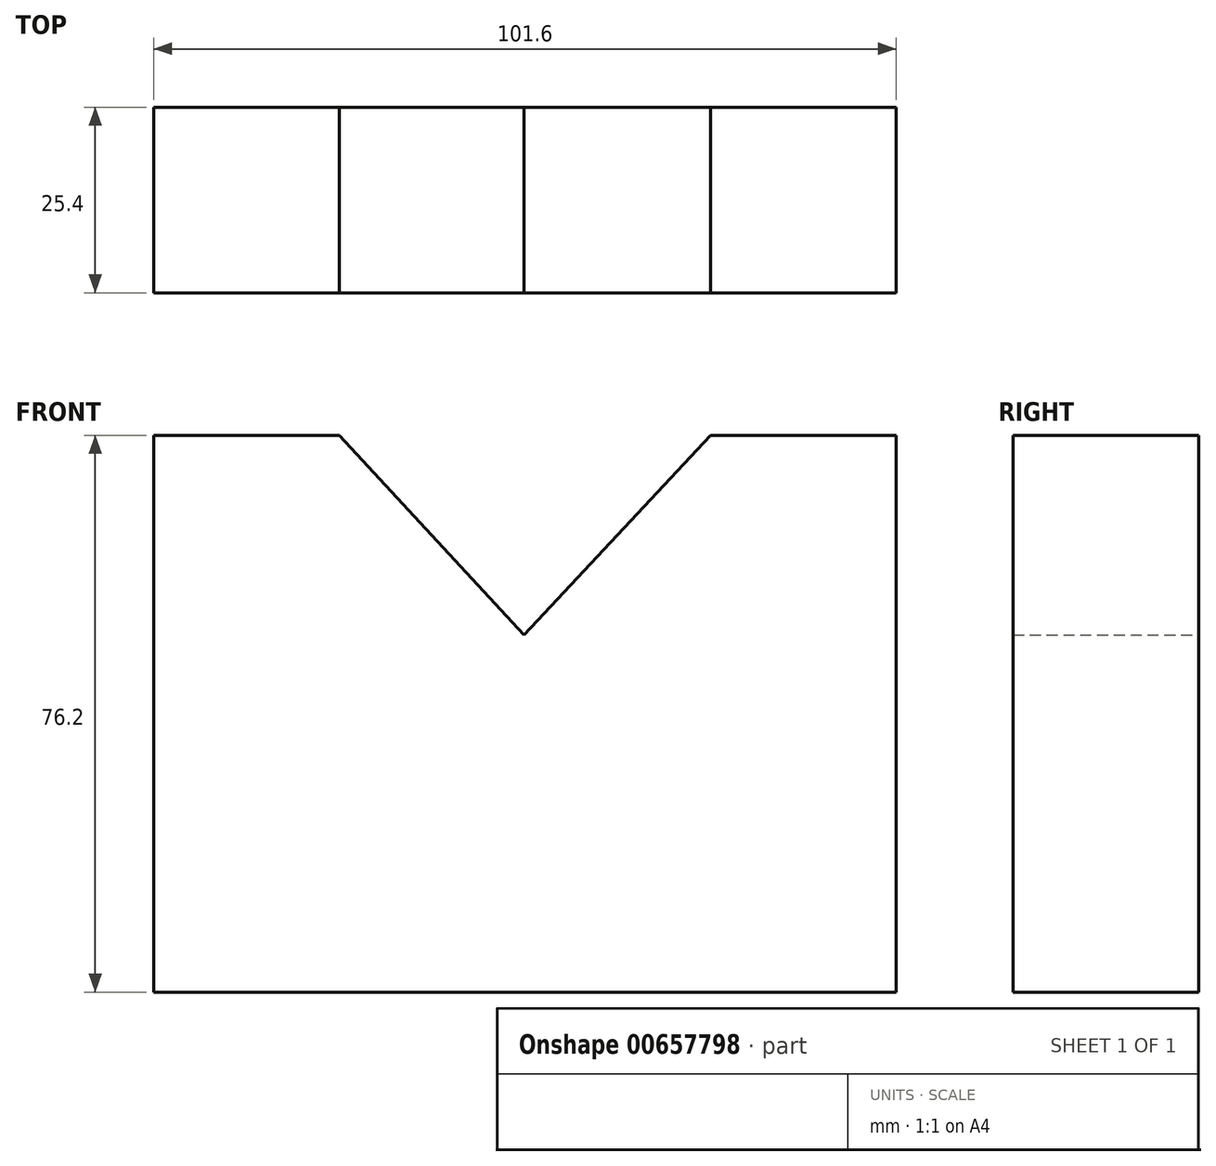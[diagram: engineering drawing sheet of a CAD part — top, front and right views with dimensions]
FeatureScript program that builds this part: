
annotation { "Feature Type Name" : "Feature", "Feature Type Description" : "" }
export const myFeature = defineFeature(function(context is Context, id is Id, definition is map)
    precondition{}
    {
        {
            var Q0;
            Q0=qCreatedBy(makeId("Front.planeOp"),FACE);
            var sketch = newSketch(context, id + "F0", { "sketchPlane" : qUnion([Q0])});
            skLineSegment(sketch, "E0", {"start": v(-61.03, -25.54) * mm, "end": v(40.57, -25.54) * mm});
            skLineSegment(sketch, "E1", {"start": v(-61.03, -25.54) * mm, "end": v(-61.03, 50.66) * mm});
            skLineSegment(sketch, "E2", {"start": v(40.57, -25.54) * mm, "end": v(40.57, 50.64) * mm});
            skLineSegment(sketch, "E3", {"start": v(-61.03, 50.66) * mm, "end": v(-35.63, 50.66) * mm});
            skLineSegment(sketch, "E4", {"start": v(40.57, 50.64) * mm, "end": v(15.17, 50.66) * mm});
            skLineSegment(sketch, "E5", {"start": v(-35.63, 50.66) * mm, "end": v(-10.37, 23.36) * mm});
            skLineSegment(sketch, "E6", {"start": v(-10.37, 23.36) * mm, "end": v(15.17, 50.66) * mm});
            skSolve(sketch);
        }
        {
            var Q0;
            Q0 = qSketchRegion(id + "F0", true);
            extrude(context, id + "F1", {"entities" : qUnion([Q0]), "depth" : 25.4 * mm, "offsetDistance" : 25.4 * mm});
        }
    });
